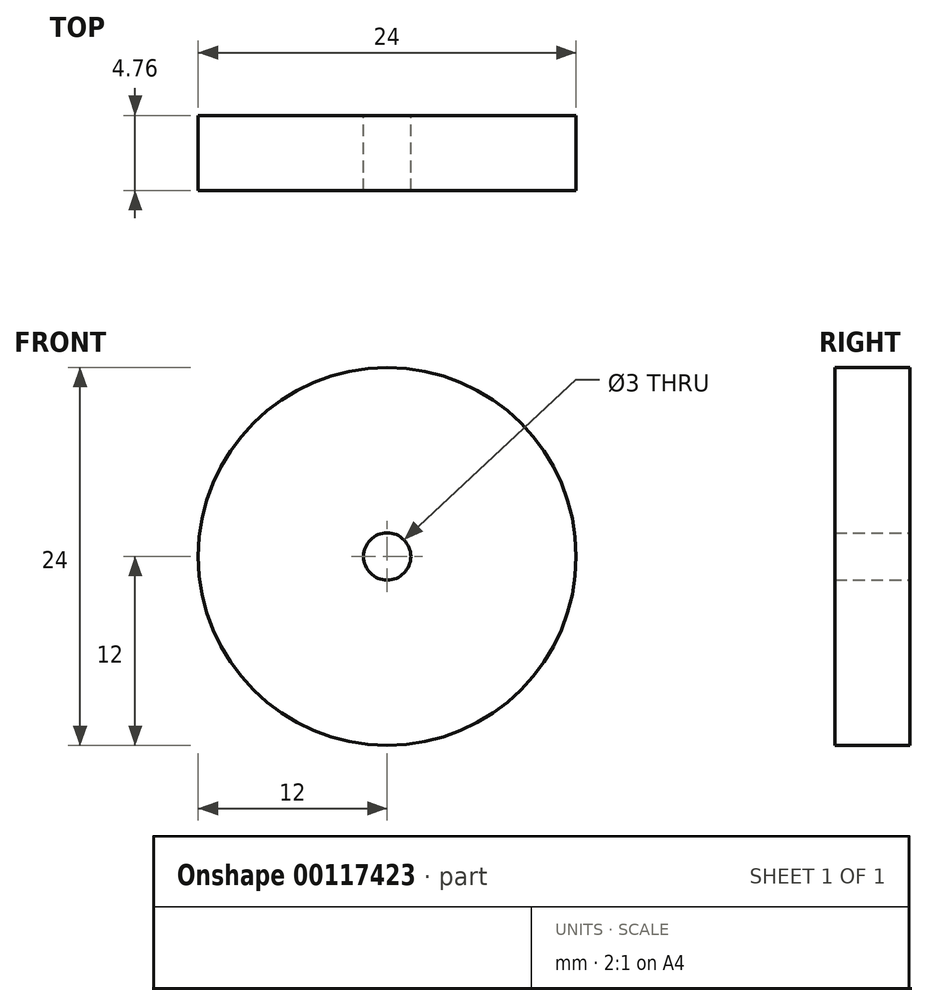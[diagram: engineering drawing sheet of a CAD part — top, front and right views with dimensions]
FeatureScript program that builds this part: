
annotation { "Feature Type Name" : "Feature", "Feature Type Description" : "" }
export const myFeature = defineFeature(function(context is Context, id is Id, definition is map)
    precondition{}
    {
        {
            var Q0;
            Q0=qCreatedBy(makeId("Front.planeOp"),FACE);
            var sketch = newSketch(context, id + "F0", { "sketchPlane" : qUnion([Q0])});
            skCircle(sketch, "E0", {"center": v(0, 0) * mm, "radius": 12 * mm});
            skCircle(sketch, "E1", {"center": v(0, 0) * mm, "radius": 1.5 * mm});
            skSolve(sketch);
        }
        {
            var Q0;
            Q0=makeQuery(id+"F0.imprint","IMPRINT",FACE,{"disambiguationData":[TD([[makeQuery(id+"F0.imprint","IMPRINT",EDGE,{"derivedFrom":sQuery(id+"F0.wireOp",EDGE,"E0")}),1.0]])]});
            var Q1;
            Q1=sQuery(id+"F0.wireOp",EDGE,"E1");
            var Q2;
            Q2=sQuery(id+"F0.wireOp",EDGE,"E0");
            extrude(context, id + "F1", {"entities" : qUnion([Q0]), "surfaceEntities" : qUnion([Q1, Q2]), "depth" : 4.76 * mm});
        }
    });
